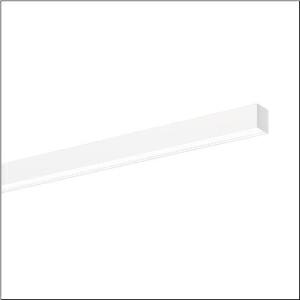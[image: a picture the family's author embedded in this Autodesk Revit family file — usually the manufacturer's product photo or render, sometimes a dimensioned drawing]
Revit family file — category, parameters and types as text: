
# Revit family: silica_r__21_51mx23db45wb_81de
name_source: partatom
category: Lighting Fixtures
units: mm (PartAtom-declared; Revit-internal decimal feet)

## family parameters
Cut with Voids When Loaded = No
Host = Face
Light Source = No
Part Type = Normal
Room Calculation Point = No
Round Connector Dimension = Use Diameter
Shared = No

## types (1)
- --- (1 x LED, 4100 lm, 28.1 W, 4000K)
    Apparent Load = 28 VA
    CIE Flux Codes = 78 96 99 100 100
    Color Rendering = 80
    Color Temperature = 4000K
    Default Elevation = 1800 mm
    Description = Silica® 21, office luminaire, primary optical cover: prismatic diffuser, of PMMA, CAT 2 (L<= 3000cd/m²), light emission: direct distribution, primary light characteristic: symmetric, installation type: surface-mounted, LED, rated luminous flux: 4.100lm, luminous efficacy: 146lm/W, light colour: 840, colour temperature: 4000K, with terminal, 3+2-pole, max. 2.5mm², mains connection: 220..240V, AC, 50/60Hz, rated input power: 28.1W, luminaire housing, of aluminium, traffic white (RAL 9016), length: 1.504mm, width: 53mm, height: 53mm, protection rating (complete): IP20, insulation class (complete): insulation class I (protective earthing), certification: CE, permissible operating ambient temperature: 0..+35°C, standard: EN 50419, packaging unit: 1 piece
    Height = 0 mm  [stored 0 ft]
    Lamp = 1 x LED
    Lamp Light Flux = 4100 lm
    Lamp Power = 28.1 W
    Lamp count = 1
    Length = 1504 mm
    Luminous efficacy = 146 lm/W
    Manufacturer = Siteco
    ModVariant = No
    Model = 51MX23DB45WB
    Mounting Place = Ceiling
    Mounting Type = Recessed
    Number of Poles = 1
    OnlyDefault = Yes
    Power Factor = 1
    Product Name = Silica® 21
    Product group = office luminaire | ceiling recessed
    ProductGroupID = 401
    Protection Class = Protection class I
    Protection Degree = IP 20
    RLX_Detail_Level = 1
    RLX_Emergency_Light_Flux = 0 lm
    RLX_Emergency_Type = 0
    RLX_Emergency_Type_DB = No
    RlxData = <blob elided: 18853 chars, md5=bc317b3e>
    Socket = socket
    Standby Power = 0 W
    System Light Flux = 4100 lm
    System Power = 28 W
    Type Comments = factory setting: luminous flux: 100 % | dim-lin: 254 | 323 mA
    Type Image = l_1313601.jpg
    URL = http://relux.com
    VarID = @adj_068359
    Voltage = 0 V
    Weight = 0.00 kg
    Width = 53 mm

note: [stored X ft] marks values corroborated as IEEE doubles in the binary element streams (Revit-internal decimal feet)

## geometry (parser evidence)
native form markers: Blend x4, Sweep x10
no freeform markers — native parametric forms only
